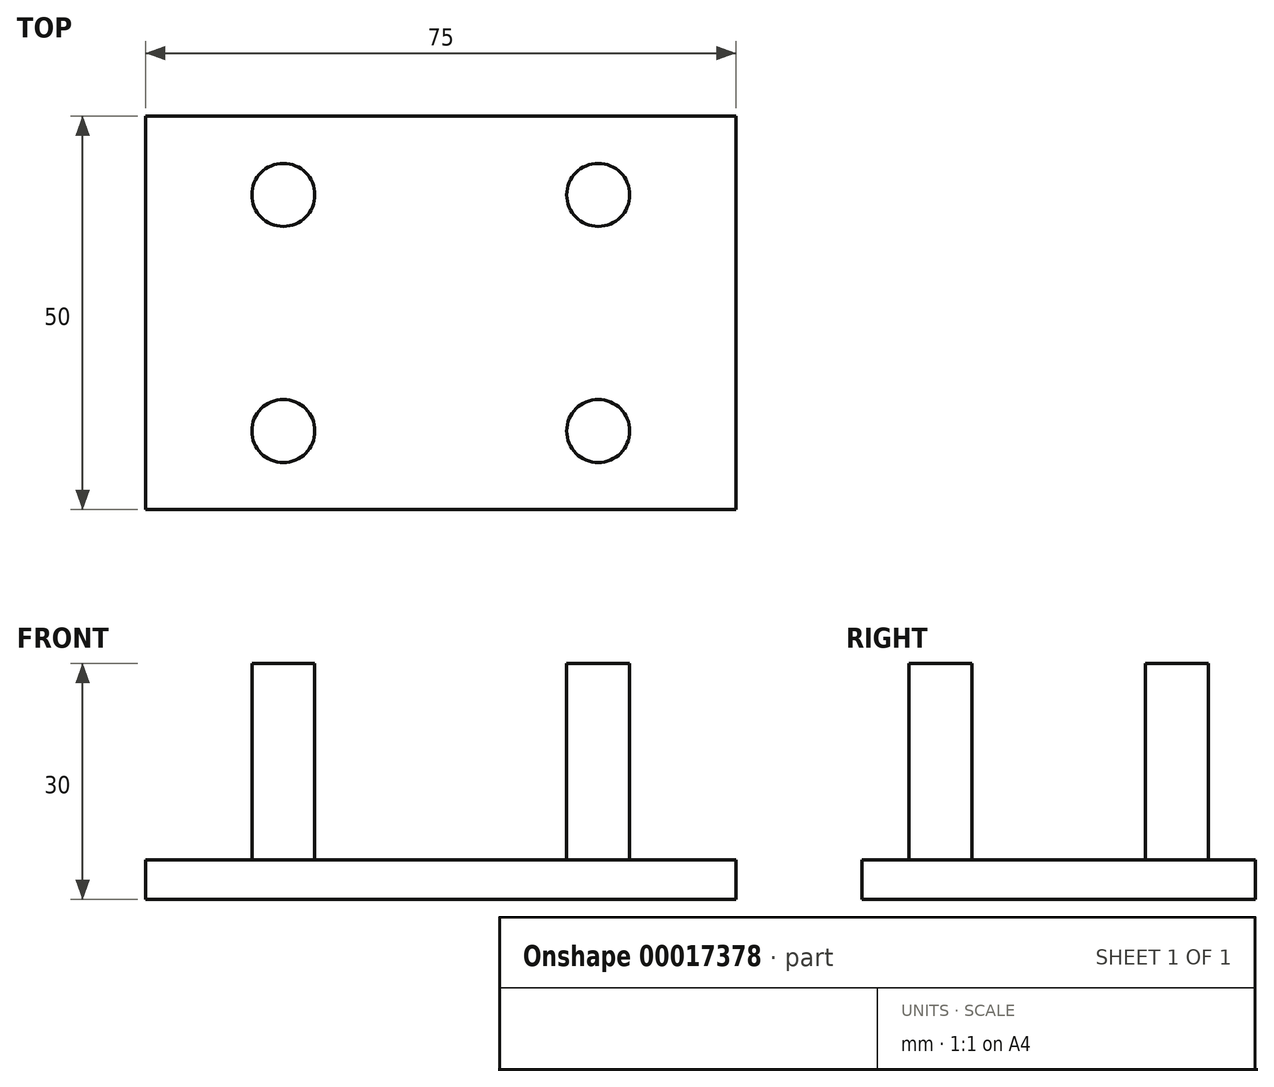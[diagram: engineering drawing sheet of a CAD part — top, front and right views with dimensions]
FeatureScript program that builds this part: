
annotation { "Feature Type Name" : "Feature", "Feature Type Description" : "" }
export const myFeature = defineFeature(function(context is Context, id is Id, definition is map)
    precondition{}
    {
        {
            var Q0;
            Q0=qCreatedBy(makeId("Top.planeOp"),FACE);
            var sketch = newSketch(context, id + "F0", { "sketchPlane" : qUnion([Q0])});
            skLineSegment(sketch, "E0.rect.bottom", {"start": v(37.5, 25) * mm, "end": v(-37.5, 25) * mm});
            skLineSegment(sketch, "E0.rect.top", {"start": v(37.5, -25) * mm, "end": v(-37.5, -25) * mm});
            skLineSegment(sketch, "E0.rect.left", {"start": v(37.5, 25) * mm, "end": v(37.5, -25) * mm});
            skLineSegment(sketch, "E0.rect.right", {"start": v(-37.5, 25) * mm, "end": v(-37.5, -25) * mm});
            skPoint(sketch, "E0.rect.middle", {"position": v(0, 0) * mm});
            skSolve(sketch);
        }
        {
            var Q0;
            Q0=qSketchRegion(id+"F0",true);
            extrude(context, id + "F1", {"entities" : qUnion([Q0]), "depth" : 5 * mm});
        }
        {
            var Q0;
            Q0=makeQuery(id+"F1.opExtrude","CAP_FACE",FACE,{"disambiguationData":[OSD([sQuery(id+"F0.wireOp",EDGE,"E0.rect.bottom"),sQuery(id+"F0.wireOp",EDGE,"E0.rect.top"),sQuery(id+"F0.wireOp",EDGE,"E0.rect.left"),sQuery(id+"F0.wireOp",EDGE,"E0.rect.right")])],"isStart":false});
            var sketch = newSketch(context, id + "F2", { "sketchPlane" : qUnion([Q0])});
            skLineSegment(sketch, "E1", {"start": v(16, 15) * mm, "end": v(20, 15) * mm});
            skLineSegment(sketch, "E2", {"start": v(20, 15) * mm, "end": v(20, 11) * mm});
            skLineSegment(sketch, "E3.0.MirrorCS", {"start": v(16, -15) * mm, "end": v(20, -15) * mm});
            skLineSegment(sketch, "E4.0.MirrorCS", {"start": v(20, -15) * mm, "end": v(20, -11) * mm});
            skCircle(sketch, "E5", {"center": v(-20, 15) * mm, "radius": 4 * mm});
            skCircle(sketch, "E6.0.MirrorC", {"center": v(20, 15) * mm, "radius": 4 * mm});
            skCircle(sketch, "E7.0.MirrorC", {"center": v(-20, -15) * mm, "radius": 4 * mm});
            skCircle(sketch, "E8.0.MirrorC", {"center": v(20, -15) * mm, "radius": 4 * mm});
            skPoint(sketch, "E9.orphan", {"position": v(0, 15) * mm});
            skPoint(sketch, "E10.orphan", {"position": v(-20, 0) * mm});
            skPoint(sketch, "E11.trimOffspring.end.orphan", {"position": v(0, -25) * mm});
            skPoint(sketch, "E12.start.orphan", {"position": v(0, 25) * mm});
            skPoint(sketch, "E13.0.MirrorCS.start.orphan", {"position": v(37.5, 0) * mm});
            skPoint(sketch, "E14.end.orphan", {"position": v(-37.5, 0) * mm});
            skSolve(sketch);
        }
        {
            var Q0;
            Q0=qSketchRegion(id+"F2",true);
            extrude(context, id + "F3", {"entities" : qUnion([Q0]), "operationType" : NewBodyOperationType.ADD, "depth" : 25 * mm});
        }
    });
